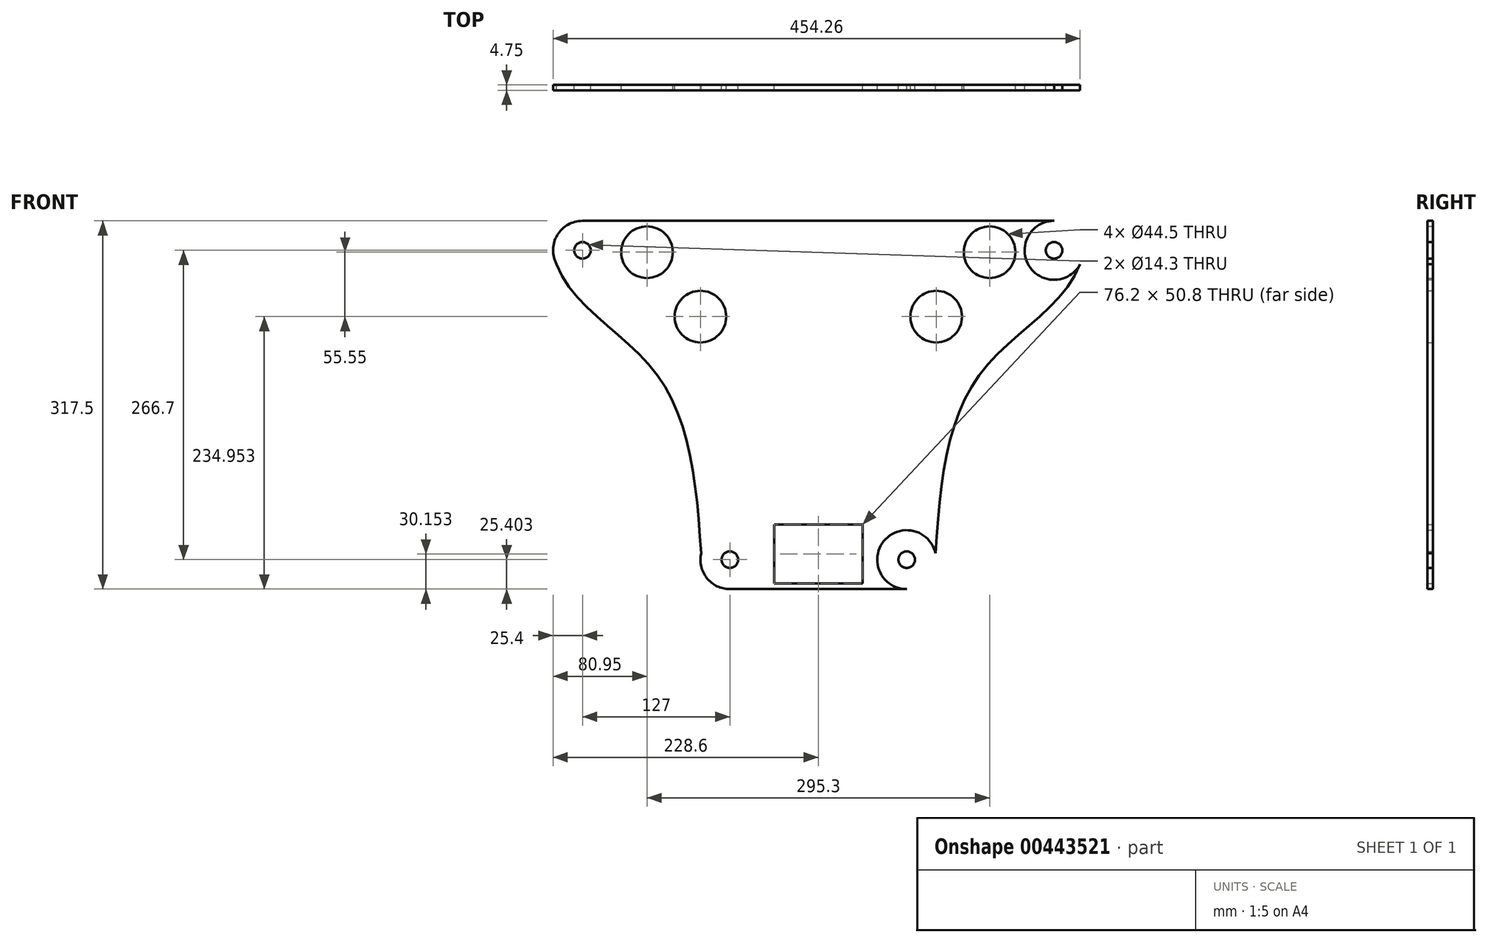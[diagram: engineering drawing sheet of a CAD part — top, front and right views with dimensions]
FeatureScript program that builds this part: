
annotation { "Feature Type Name" : "Feature", "Feature Type Description" : "" }
export const myFeature = defineFeature(function(context is Context, id is Id, definition is map)
    precondition{}
    {
        {
            var Q0;
            Q0=qCreatedBy(makeId("Front.planeOp"),FACE);
            var sketch = newSketch(context, id + "F0", { "sketchPlane" : qUnion([Q0])});
            skCircle(sketch, "E0", {"center": v(-203.2, 106.28) * mm, "radius": 25.4 * mm});
            skCircle(sketch, "E1", {"center": v(-76.2, -160.42) * mm, "radius": 25.4 * mm});
            skCircle(sketch, "E2", {"center": v(-76.2, -160.42) * mm, "radius": 7.15 * mm});
            skCircle(sketch, "E3", {"center": v(-203.2, 106.28) * mm, "radius": 7.15 * mm});
            skCircle(sketch, "E4.MirrorC", {"center": v(203.2, 106.28) * mm, "radius": 25.4 * mm});
            skCircle(sketch, "E5.MirrorC", {"center": v(203.2, 106.28) * mm, "radius": 7.15 * mm});
            skCircle(sketch, "E6.MirrorC", {"center": v(76.2, -160.42) * mm, "radius": 25.4 * mm});
            skCircle(sketch, "E7.MirrorC", {"center": v(76.2, -160.42) * mm, "radius": 7.15 * mm});
            skLineSegment(sketch, "E8", {"start": v(-203.2, 131.68) * mm, "end": v(203.2, 131.68) * mm});
            skFitSpline(sketch, "E9", {"points": [v(-225.66, 94.42) * mm, v(-139.7, 0) * mm, v(-101.02, -155.03) * mm], "startDerivative": vector(93.9, -244.25) * mm, "endDerivative": vector(21.65, -345.52) * mm});
            skLineSegment(sketch, "E10", {"start": v(-76.2, -185.82) * mm, "end": v(76.2, -185.82) * mm});
            skFitSpline(sketch, "E11.MirrorCS", {"points": [v(225.66, 94.42) * mm, v(139.7, 0) * mm, v(101.02, -155.03) * mm], "startDerivative": vector(-93.9, -244.25) * mm, "endDerivative": vector(-21.65, -345.52) * mm});
            skCircle(sketch, "E12", {"center": v(-147.65, 104.68) * mm, "radius": 22.25 * mm});
            skCircle(sketch, "E13", {"center": v(-101.6, 49.13) * mm, "radius": 7.15 * mm});
            skCircle(sketch, "E14.MirrorC", {"center": v(147.65, 104.68) * mm, "radius": 22.25 * mm});
            skCircle(sketch, "E15.MirrorC", {"center": v(101.6, 49.13) * mm, "radius": 7.15 * mm});
            skLineSegment(sketch, "E16.bottom", {"start": v(0, -130.27) * mm, "end": v(-38.1, -130.27) * mm});
            skLineSegment(sketch, "E16.top", {"start": v(0, -181.07) * mm, "end": v(-38.1, -181.07) * mm});
            skLineSegment(sketch, "E16.right", {"start": v(-38.1, -130.27) * mm, "end": v(-38.1, -181.07) * mm});
            skLineSegment(sketch, "E17.MirrorCS", {"start": v(0, -130.27) * mm, "end": v(38.1, -130.27) * mm});
            skLineSegment(sketch, "E18.MirrorCS", {"start": v(38.1, -130.27) * mm, "end": v(38.1, -181.07) * mm});
            skLineSegment(sketch, "E19.MirrorCS", {"start": v(0, -181.07) * mm, "end": v(38.1, -181.07) * mm});
            skCircle(sketch, "E20", {"center": v(-101.6, 49.13) * mm, "radius": 22.25 * mm});
            skCircle(sketch, "E21.MirrorC", {"center": v(101.6, 49.13) * mm, "radius": 22.25 * mm});
            skSolve(sketch);
        }
        {
            var Q0;
            {var subQ2=sQuery(id+"F0.wireOp",EDGE,"E8");Q0=makeQuery(id+"F0.imprint","IMPRINT",FACE,{"disambiguationData":[TD([[makeQuery(id+"F0.imprint","IMPRINT",EDGE,{"derivedFrom":subQ2}),-1.0]])]});}
            var Q1;
            Q1=makeQuery(id+"F0.imprint","IMPRINT",FACE,{"disambiguationData":[TD([[makeQuery(id+"F0.imprint","IMPRINT",EDGE,{"derivedFrom":sQuery(id+"F0.wireOp",EDGE,"E7.MirrorC")}),1.0]])]});
            var Q2;
            Q2=makeQuery(id+"F0.imprint","IMPRINT",FACE,{"disambiguationData":[TD([[makeQuery(id+"F0.imprint","IMPRINT",EDGE,{"derivedFrom":sQuery(id+"F0.wireOp",EDGE,"E2")}),-1.0]])]});
            var Q3;
            Q3=makeQuery(id+"F0.imprint","IMPRINT",FACE,{"disambiguationData":[TD([[makeQuery(id+"F0.imprint","IMPRINT",EDGE,{"derivedFrom":sQuery(id+"F0.wireOp",EDGE,"E3")}),-1.0]])]});
            var Q4;
            Q4=makeQuery(id+"F0.imprint","IMPRINT",FACE,{"disambiguationData":[TD([[makeQuery(id+"F0.imprint","IMPRINT",EDGE,{"derivedFrom":sQuery(id+"F0.wireOp",EDGE,"E5.MirrorC")}),1.0]])]});
            extrude(context, id + "F1", {"entities" : qUnion([Q0, Q1, Q2, Q3, Q4]), "depth" : 4.75 * mm});
        }
    });
